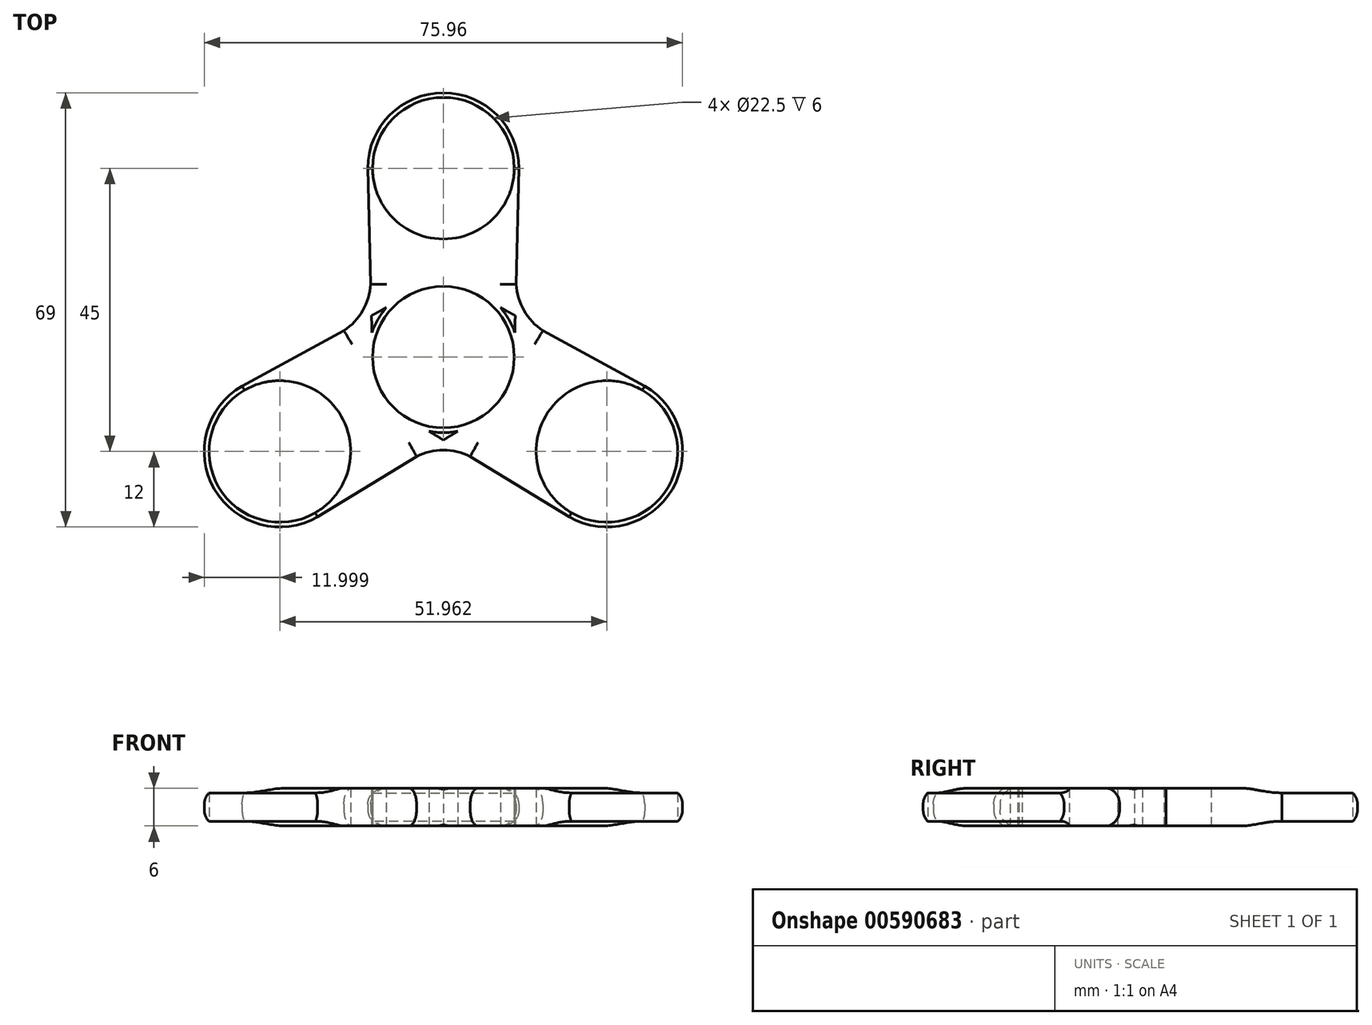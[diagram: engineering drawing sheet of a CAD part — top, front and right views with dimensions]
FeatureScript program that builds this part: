
annotation { "Feature Type Name" : "Feature", "Feature Type Description" : "" }
export const myFeature = defineFeature(function(context is Context, id is Id, definition is map)
    precondition{}
    {
        {
            var Q0;
            Q0=qCreatedBy(makeId("Top.planeOp"),FACE);
            var sketch = newSketch(context, id + "F0", { "sketchPlane" : qUnion([Q0])});
            skCircle(sketch, "E0", {"center": v(0, 0) * mm, "radius": 11.25 * mm});
            skCircle(sketch, "E1", {"center": v(0, 0) * mm, "radius": 12 * mm});
            skLineSegment(sketch, "E2", {"start": v(0, 0) * mm, "end": v(0, 12) * mm, "construction": true});
            skCircle(sketch, "E3", {"center": v(0, 30) * mm, "radius": 11.25 * mm});
            skArc(sketch, "E4", {"start": v(11.99, 29.4) * mm, "mid": v(0, 42) * mm, "end": v(-11.99, 29.4) * mm});
            skLineSegment(sketch, "E5", {"start": v(-11.25, 30) * mm, "end": v(-12, 30) * mm, "construction": true});
            skLineSegment(sketch, "E6", {"start": v(-12, 30) * mm, "end": v(-11.25, 30) * mm, "construction": true});
            skLineSegment(sketch, "E7", {"start": v(-11.25, 0) * mm, "end": v(-12, 30) * mm});
            skLineSegment(sketch, "E8", {"start": v(11.25, 0) * mm, "end": v(12, 30) * mm});
            skLineSegment(sketch, "E9.trimOffspring", {"start": v(11.25, 30) * mm, "end": v(12, 30) * mm, "construction": true});
            skLineSegment(sketch, "E10", {"start": v(0, 0) * mm, "end": v(9.74, -5.63) * mm, "construction": true});
            skLineSegment(sketch, "E11", {"start": v(0, 0) * mm, "end": v(-9.74, -5.62) * mm, "construction": true});
            skLineSegment(sketch, "E12", {"start": v(0, 0) * mm, "end": v(10.4, -6) * mm, "construction": true});
            skCircle(sketch, "E13", {"center": v(25.98, -15) * mm, "radius": 11.25 * mm});
            skArc(sketch, "E14", {"start": v(19.98, -25.4) * mm, "mid": v(36.52, -20.74) * mm, "end": v(31.45, -4.32) * mm});
            skLineSegment(sketch, "E15", {"start": v(31.6, -5.26) * mm, "end": v(31.98, -4.6) * mm, "construction": true});
            skLineSegment(sketch, "E16", {"start": v(31.98, -4.6) * mm, "end": v(31.6, -5.26) * mm, "construction": true});
            skLineSegment(sketch, "E17", {"start": v(0, 0) * mm, "end": v(11.25, 0) * mm, "construction": true});
            skLineSegment(sketch, "E18", {"start": v(0, 0) * mm, "end": v(-5.63, -9.74) * mm, "construction": true});
            skLineSegment(sketch, "E19", {"start": v(-5.63, -9.74) * mm, "end": v(5.63, 9.74) * mm, "construction": true});
            skLineSegment(sketch, "E20", {"start": v(5.62, 9.74) * mm, "end": v(31.98, -4.6) * mm});
            skLineSegment(sketch, "E21", {"start": v(-5.63, -9.74) * mm, "end": v(19.98, -25.4) * mm});
            skLineSegment(sketch, "E22.trimOffspring", {"start": v(20.36, -24.74) * mm, "end": v(19.98, -25.4) * mm, "construction": true});
            skLineSegment(sketch, "E23", {"start": v(0, 0) * mm, "end": v(-25.98, -15) * mm, "construction": true});
            skLineSegment(sketch, "E24", {"start": v(0, 0) * mm, "end": v(0, 30) * mm, "construction": true});
            skLineSegment(sketch, "E25", {"start": v(0, 0) * mm, "end": v(25.98, -15) * mm, "construction": true});
            skCircle(sketch, "E26", {"center": v(-25.98, -15) * mm, "radius": 11.25 * mm});
            skCircle(sketch, "E27", {"center": v(-25.98, -15) * mm, "radius": 12 * mm});
            skLineSegment(sketch, "E28", {"start": v(0, 0) * mm, "end": v(-5.62, 9.74) * mm, "construction": true});
            skLineSegment(sketch, "E29", {"start": v(-5.62, 9.74) * mm, "end": v(5.62, -9.74) * mm, "construction": true});
            skLineSegment(sketch, "E30", {"start": v(-25.98, -15) * mm, "end": v(-19.98, -25.4) * mm, "construction": true});
            skLineSegment(sketch, "E31", {"start": v(-25.98, -15) * mm, "end": v(-31.98, -4.6) * mm, "construction": true});
            skLineSegment(sketch, "E32", {"start": v(5.63, -9.74) * mm, "end": v(-19.98, -25.4) * mm});
            skLineSegment(sketch, "E33", {"start": v(-31.98, -4.6) * mm, "end": v(-5.63, 9.74) * mm});
            skLineSegment(sketch, "E34", {"start": v(-11.41, 6.6) * mm, "end": v(-11.54, 11.59) * mm, "construction": true});
            skLineSegment(sketch, "E35", {"start": v(-11.41, 6.6) * mm, "end": v(-15.8, 4.2) * mm, "construction": true});
            skLineSegment(sketch, "E36", {"start": v(11.41, 6.6) * mm, "end": v(11.54, 11.59) * mm, "construction": true});
            skLineSegment(sketch, "E37", {"start": v(11.41, 6.6) * mm, "end": v(15.8, 4.2) * mm, "construction": true});
            skLineSegment(sketch, "E38", {"start": v(0, -13.18) * mm, "end": v(-4.27, -15.79) * mm, "construction": true});
            skLineSegment(sketch, "E39", {"start": v(0, -13.18) * mm, "end": v(4.27, -15.79) * mm, "construction": true});
            skArc(sketch, "E40", {"start": v(-15.8, 4.2) * mm, "mid": v(-12.81, 7.4) * mm, "end": v(-11.54, 11.59) * mm});
            skPoint(sketch, "E41.end.orphan", {"position": v(-12.81, 7.4) * mm});
            skPoint(sketch, "E42.end.orphan", {"position": v(-13.67, 7.9) * mm});
            skArc(sketch, "E43", {"start": v(11.54, 11.59) * mm, "mid": v(12.81, 7.4) * mm, "end": v(15.8, 4.2) * mm});
            skPoint(sketch, "E44.end.orphan", {"position": v(12.81, 7.4) * mm});
            skPoint(sketch, "E45.start.orphan", {"position": v(13.67, 7.9) * mm});
            skArc(sketch, "E46", {"start": v(4.27, -15.79) * mm, "mid": v(0, -14.8) * mm, "end": v(-4.27, -15.79) * mm});
            skPoint(sketch, "E47.start.orphan", {"position": v(0, -15.79) * mm});
            skSolve(sketch);
        }
        {
            var Q0;
            Q0=makeQuery(id+"F0.imprint","IMPRINT",FACE,{"disambiguationData":[TD([[makeQuery(id+"F0.imprint","IMPRINT",EDGE,{"derivedFrom":sQuery(id+"F0.wireOp",EDGE,"E13")}),-1.0]])]});
            var Q1;
            {var subQ7=sQuery(id+"F0.wireOp",EDGE,"E1");var subQ9=sQuery(id+"F0.wireOp",EDGE,"E7");var subQ11=makeQuery(id+"F0.imprint","INTERSECT",VERTEX,{"derivedFrom":[subQ7,subQ9]});Q1=makeQuery(id+"F0.imprint","IMPRINT",FACE,{"disambiguationData":[TD([[makeQuery(id+"F0.imprint","IMPRINT",EDGE,{"disambiguationData":[TD([[subQ11,-1.0]])],"derivedFrom":subQ7}),-1.0]])]});}
            var Q2;
            Q2=makeQuery(id+"F0.imprint","IMPRINT",FACE,{"disambiguationData":[TD([[makeQuery(id+"F0.imprint","IMPRINT",EDGE,{"derivedFrom":sQuery(id+"F0.wireOp",EDGE,"E3")}),-1.0]])]});
            var Q3;
            Q3=makeQuery(id+"F0.imprint","IMPRINT",FACE,{"disambiguationData":[TD([[makeQuery(id+"F0.imprint","IMPRINT",EDGE,{"derivedFrom":sQuery(id+"F0.wireOp",EDGE,"E26")}),-1.0]])]});
            var Q4;
            {var subQ0=sQuery(id+"F0.wireOp",EDGE,"LzCppDYF-5cjn-ystm-teWX-WIOvTmqxfPc8");Q4=makeQuery(id+"F0.imprint","IMPRINT",FACE,{"disambiguationData":[TD([[makeQuery(id+"F0.imprint","IMPRINT",EDGE,{"derivedFrom":subQ0}),-1.0]])]});}
            var Q5;
            {var subQ0=sQuery(id+"F0.wireOp",EDGE,"E45");Q5=makeQuery(id+"F0.imprint","IMPRINT",FACE,{"disambiguationData":[TD([[makeQuery(id+"F0.imprint","IMPRINT",EDGE,{"derivedFrom":subQ0}),-1.0]])]});}
            var Q6;
            {var subQ0=sQuery(id+"F0.wireOp",EDGE,"dLhTZdyE-zlHB-rUEX-3xYo-1x3OKXFwP9mY");Q6=makeQuery(id+"F0.imprint","IMPRINT",FACE,{"disambiguationData":[TD([[makeQuery(id+"F0.imprint","IMPRINT",EDGE,{"derivedFrom":subQ0}),1.0]])]});}
            var Q7;
            {var subQ0=sQuery(id+"F0.wireOp",EDGE,"E46");Q7=makeQuery(id+"F0.imprint","IMPRINT",FACE,{"disambiguationData":[TD([[makeQuery(id+"F0.imprint","IMPRINT",EDGE,{"derivedFrom":subQ0}),-1.0]])]});}
            var Q8;
            {var subQ0=sQuery(id+"F0.wireOp",EDGE,"E40");Q8=makeQuery(id+"F0.imprint","IMPRINT",FACE,{"disambiguationData":[TD([[makeQuery(id+"F0.imprint","IMPRINT",EDGE,{"derivedFrom":subQ0}),-1.0]])]});}
            var Q9;
            {var subQ0=sQuery(id+"F0.wireOp",EDGE,"E43");Q9=makeQuery(id+"F0.imprint","IMPRINT",FACE,{"disambiguationData":[TD([[makeQuery(id+"F0.imprint","IMPRINT",EDGE,{"derivedFrom":subQ0}),-1.0]])]});}
            var Q10;
            {var subQ0=sQuery(id+"F0.wireOp",EDGE,"E7");var subQ1=sQuery(id+"F0.wireOp",EDGE,"E0");var subQ2=makeQuery(id+"F0.imprint","INTERSECT",VERTEX,{"derivedFrom":[subQ1,subQ0]});Q10=makeQuery(id+"F0.imprint","IMPRINT",FACE,{"disambiguationData":[TD([[makeQuery(id+"F0.imprint","IMPRINT",EDGE,{"disambiguationData":[TD([[subQ2,-1.0]])],"derivedFrom":subQ1}),-1.0]])]});}
            var Q11;
            {var subQ0=sQuery(id+"F0.wireOp",EDGE,"E7");var subQ1=sQuery(id+"F0.wireOp",EDGE,"E0");var subQ2=makeQuery(id+"F0.imprint","INTERSECT",VERTEX,{"derivedFrom":[subQ1,subQ0]});Q11=makeQuery(id+"F0.imprint","IMPRINT",FACE,{"disambiguationData":[TD([[makeQuery(id+"F0.imprint","IMPRINT",EDGE,{"disambiguationData":[TD([[subQ2,1.0]])],"derivedFrom":subQ1}),-1.0]])]});}
            var Q12;
            {var subQ0=sQuery(id+"F0.wireOp",EDGE,"E20");var subQ1=sQuery(id+"F0.wireOp",EDGE,"E0");var subQ2=makeQuery(id+"F0.imprint","INTERSECT",VERTEX,{"derivedFrom":[subQ1,subQ0]});Q12=makeQuery(id+"F0.imprint","IMPRINT",FACE,{"disambiguationData":[TD([[makeQuery(id+"F0.imprint","IMPRINT",EDGE,{"disambiguationData":[TD([[subQ2,-1.0]])],"derivedFrom":subQ1}),-1.0]])]});}
            var Q13;
            {var subQ0=sQuery(id+"F0.wireOp",EDGE,"E8");var subQ1=sQuery(id+"F0.wireOp",EDGE,"E0");var subQ2=makeQuery(id+"F0.imprint","INTERSECT",VERTEX,{"derivedFrom":[subQ1,subQ0]});Q13=makeQuery(id+"F0.imprint","IMPRINT",FACE,{"disambiguationData":[TD([[makeQuery(id+"F0.imprint","IMPRINT",EDGE,{"disambiguationData":[TD([[subQ2,-1.0]])],"derivedFrom":subQ1}),-1.0]])]});}
            var Q14;
            {var subQ0=sQuery(id+"F0.wireOp",EDGE,"E8");var subQ1=sQuery(id+"F0.wireOp",EDGE,"E0");var subQ2=makeQuery(id+"F0.imprint","INTERSECT",VERTEX,{"derivedFrom":[subQ1,subQ0]});Q14=makeQuery(id+"F0.imprint","IMPRINT",FACE,{"disambiguationData":[TD([[makeQuery(id+"F0.imprint","IMPRINT",EDGE,{"disambiguationData":[TD([[subQ2,1.0]])],"derivedFrom":subQ1}),-1.0]])]});}
            var Q15;
            {var subQ0=sQuery(id+"F0.wireOp",EDGE,"E21");var subQ1=sQuery(id+"F0.wireOp",EDGE,"E0");var subQ2=makeQuery(id+"F0.imprint","INTERSECT",VERTEX,{"derivedFrom":[subQ1,subQ0]});Q15=makeQuery(id+"F0.imprint","IMPRINT",FACE,{"disambiguationData":[TD([[makeQuery(id+"F0.imprint","IMPRINT",EDGE,{"disambiguationData":[TD([[subQ2,-1.0]])],"derivedFrom":subQ1}),-1.0]])]});}
            extrude(context, id + "F1", {"entities" : qUnion([Q0, Q1, Q2, Q3, Q4, Q5, Q6, Q7, Q8, Q9, Q10, Q11, Q12, Q13, Q14, Q15]), "depth" : 6 * mm, "offsetDistance" : 25.4 * mm});
        }
        {
            var Q0;
            {var subQ0=sQuery(id+"F0.wireOp",EDGE,"E33");var subQ1=sQuery(id+"F0.wireOp",EDGE,"E27");Q0=makeQuery(id+"F1.opExtrude","CAP_EDGE",EDGE,{"disambiguationData":[OSD([subQ0]),TDD([makeQuery(id+"F0.imprint","IMPRINT",EDGE,{"disambiguationData":[TD([[makeQuery(id+"F0.imprint","INTERSECT",VERTEX,{"disambiguationData":[OD(0.0)],"derivedFrom":[subQ1,subQ0]}),-1.0]])],"derivedFrom":subQ0}),makeQuery(id+"F0.imprint","IMPRINT",EDGE,{"disambiguationData":[TD([[makeQuery(id+"F0.imprint","INTERSECT",VERTEX,{"derivedFrom":[subQ0,sQuery(id+"F0.wireOp",EDGE,"E40")]}),1.0]])],"derivedFrom":subQ0})])],"isStart":false});}
            var Q1;
            Q1=makeQuery(id+"F1.opExtrude","CAP_EDGE",EDGE,{"disambiguationData":[OSD([sQuery(id+"F0.wireOp",EDGE,"E40")])],"isStart":false});
            var Q2;
            {var subQ0=sQuery(id+"F0.wireOp",EDGE,"E7");var subQ1=sQuery(id+"F0.wireOp",EDGE,"E4");var subQ2=makeQuery(id+"F0.imprint","INTERSECT",VERTEX,{"disambiguationData":[OD(0.0)],"derivedFrom":[subQ1,subQ0]});Q2=makeQuery(id+"F1.opExtrude","CAP_EDGE",EDGE,{"disambiguationData":[OSD([subQ0]),TDD([makeQuery(id+"F0.imprint","IMPRINT",EDGE,{"disambiguationData":[TD([[subQ2,1.0]])],"derivedFrom":subQ0}),makeQuery(id+"F0.imprint","IMPRINT",EDGE,{"disambiguationData":[TD([[subQ2,-1.0]])],"derivedFrom":subQ0})])],"isStart":false});}
            var Q3;
            Q3=makeQuery(id+"F1.opExtrude","CAP_EDGE",EDGE,{"disambiguationData":[OSD([sQuery(id+"F0.wireOp",EDGE,"E4")])],"isStart":false});
            var Q4;
            {var subQ0=sQuery(id+"F0.wireOp",EDGE,"E8");var subQ1=sQuery(id+"F0.wireOp",EDGE,"E4");var subQ2=makeQuery(id+"F0.imprint","INTERSECT",VERTEX,{"disambiguationData":[OD(0.0)],"derivedFrom":[subQ1,subQ0]});Q4=makeQuery(id+"F1.opExtrude","CAP_EDGE",EDGE,{"disambiguationData":[OSD([subQ0]),TDD([makeQuery(id+"F0.imprint","IMPRINT",EDGE,{"disambiguationData":[TD([[subQ2,1.0]])],"derivedFrom":subQ0}),makeQuery(id+"F0.imprint","IMPRINT",EDGE,{"disambiguationData":[TD([[subQ2,-1.0]])],"derivedFrom":subQ0})])],"isStart":false});}
            var Q5;
            Q5=makeQuery(id+"F1.opExtrude","CAP_EDGE",EDGE,{"disambiguationData":[OSD([sQuery(id+"F0.wireOp",EDGE,"E43")])],"isStart":false});
            var Q6;
            {var subQ0=sQuery(id+"F0.wireOp",EDGE,"E20");var subQ1=sQuery(id+"F0.wireOp",EDGE,"E14");var subQ2=makeQuery(id+"F0.imprint","INTERSECT",VERTEX,{"disambiguationData":[OD(0.0)],"derivedFrom":[subQ1,subQ0]});Q6=makeQuery(id+"F1.opExtrude","CAP_EDGE",EDGE,{"disambiguationData":[OSD([subQ0]),TDD([makeQuery(id+"F0.imprint","IMPRINT",EDGE,{"disambiguationData":[TD([[subQ2,1.0]])],"derivedFrom":subQ0}),makeQuery(id+"F0.imprint","IMPRINT",EDGE,{"disambiguationData":[TD([[subQ2,-1.0]])],"derivedFrom":subQ0})])],"isStart":false});}
            var Q7;
            Q7=makeQuery(id+"F1.opExtrude","CAP_EDGE",EDGE,{"disambiguationData":[OSD([sQuery(id+"F0.wireOp",EDGE,"E14")])],"isStart":false});
            var Q8;
            {var subQ0=sQuery(id+"F0.wireOp",EDGE,"E21");Q8=makeQuery(id+"F1.opExtrude","CAP_EDGE",EDGE,{"disambiguationData":[OSD([subQ0]),TDD([makeQuery(id+"F0.imprint","IMPRINT",EDGE,{"disambiguationData":[TD([[makeQuery(id+"F0.imprint","INTERSECT",VERTEX,{"derivedFrom":[sQuery(id+"F0.wireOp",EDGE,"E14"),subQ0]}),1.0]])],"derivedFrom":subQ0})])],"isStart":false});}
            var Q9;
            Q9=makeQuery(id+"F1.opExtrude","CAP_EDGE",EDGE,{"disambiguationData":[OSD([sQuery(id+"F0.wireOp",EDGE,"E46")])],"isStart":false});
            var Q10;
            {var subQ0=sQuery(id+"F0.wireOp",EDGE,"E32");var subQ1=sQuery(id+"F0.wireOp",EDGE,"E27");Q10=makeQuery(id+"F1.opExtrude","CAP_EDGE",EDGE,{"disambiguationData":[OSD([subQ0]),TDD([makeQuery(id+"F0.imprint","IMPRINT",EDGE,{"disambiguationData":[TD([[makeQuery(id+"F0.imprint","INTERSECT",VERTEX,{"derivedFrom":[subQ0,sQuery(id+"F0.wireOp",EDGE,"E46")]}),-1.0]])],"derivedFrom":subQ0}),makeQuery(id+"F0.imprint","IMPRINT",EDGE,{"disambiguationData":[TD([[makeQuery(id+"F0.imprint","INTERSECT",VERTEX,{"disambiguationData":[OD(0.0)],"derivedFrom":[subQ1,subQ0]}),1.0]])],"derivedFrom":subQ0})])],"isStart":false});}
            var Q11;
            Q11=makeQuery(id+"F1.opExtrude","CAP_EDGE",EDGE,{"disambiguationData":[OSD([sQuery(id+"F0.wireOp",EDGE,"E27")])],"isStart":false});
            var Q12;
            Q12=makeQuery(id+"F1.opExtrude","CAP_EDGE",EDGE,{"disambiguationData":[OSD([sQuery(id+"F0.wireOp",EDGE,"E4")])],"isStart":true});
            var Q13;
            {var subQ0=sQuery(id+"F0.wireOp",EDGE,"E7");var subQ1=sQuery(id+"F0.wireOp",EDGE,"E4");var subQ2=makeQuery(id+"F0.imprint","INTERSECT",VERTEX,{"disambiguationData":[OD(0.0)],"derivedFrom":[subQ1,subQ0]});Q13=makeQuery(id+"F1.opExtrude","CAP_EDGE",EDGE,{"disambiguationData":[OSD([subQ0]),TDD([makeQuery(id+"F0.imprint","IMPRINT",EDGE,{"disambiguationData":[TD([[subQ2,1.0]])],"derivedFrom":subQ0}),makeQuery(id+"F0.imprint","IMPRINT",EDGE,{"disambiguationData":[TD([[subQ2,-1.0]])],"derivedFrom":subQ0})])],"isStart":true});}
            var Q14;
            Q14=makeQuery(id+"F1.opExtrude","CAP_EDGE",EDGE,{"disambiguationData":[OSD([sQuery(id+"F0.wireOp",EDGE,"E40")])],"isStart":true});
            var Q15;
            {var subQ0=sQuery(id+"F0.wireOp",EDGE,"E33");var subQ1=sQuery(id+"F0.wireOp",EDGE,"E27");Q15=makeQuery(id+"F1.opExtrude","CAP_EDGE",EDGE,{"disambiguationData":[OSD([subQ0]),TDD([makeQuery(id+"F0.imprint","IMPRINT",EDGE,{"disambiguationData":[TD([[makeQuery(id+"F0.imprint","INTERSECT",VERTEX,{"disambiguationData":[OD(0.0)],"derivedFrom":[subQ1,subQ0]}),-1.0]])],"derivedFrom":subQ0}),makeQuery(id+"F0.imprint","IMPRINT",EDGE,{"disambiguationData":[TD([[makeQuery(id+"F0.imprint","INTERSECT",VERTEX,{"derivedFrom":[subQ0,sQuery(id+"F0.wireOp",EDGE,"E40")]}),1.0]])],"derivedFrom":subQ0})])],"isStart":true});}
            var Q16;
            Q16=makeQuery(id+"F1.opExtrude","CAP_EDGE",EDGE,{"disambiguationData":[OSD([sQuery(id+"F0.wireOp",EDGE,"E27")])],"isStart":true});
            var Q17;
            {var subQ0=sQuery(id+"F0.wireOp",EDGE,"E32");var subQ1=sQuery(id+"F0.wireOp",EDGE,"E27");Q17=makeQuery(id+"F1.opExtrude","CAP_EDGE",EDGE,{"disambiguationData":[OSD([subQ0]),TDD([makeQuery(id+"F0.imprint","IMPRINT",EDGE,{"disambiguationData":[TD([[makeQuery(id+"F0.imprint","INTERSECT",VERTEX,{"derivedFrom":[subQ0,sQuery(id+"F0.wireOp",EDGE,"E46")]}),-1.0]])],"derivedFrom":subQ0}),makeQuery(id+"F0.imprint","IMPRINT",EDGE,{"disambiguationData":[TD([[makeQuery(id+"F0.imprint","INTERSECT",VERTEX,{"disambiguationData":[OD(0.0)],"derivedFrom":[subQ1,subQ0]}),1.0]])],"derivedFrom":subQ0})])],"isStart":true});}
            var Q18;
            Q18=makeQuery(id+"F1.opExtrude","CAP_EDGE",EDGE,{"disambiguationData":[OSD([sQuery(id+"F0.wireOp",EDGE,"E46")])],"isStart":true});
            var Q19;
            {var subQ0=sQuery(id+"F0.wireOp",EDGE,"E21");Q19=makeQuery(id+"F1.opExtrude","CAP_EDGE",EDGE,{"disambiguationData":[OSD([subQ0]),TDD([makeQuery(id+"F0.imprint","IMPRINT",EDGE,{"disambiguationData":[TD([[makeQuery(id+"F0.imprint","INTERSECT",VERTEX,{"derivedFrom":[sQuery(id+"F0.wireOp",EDGE,"E14"),subQ0]}),1.0]])],"derivedFrom":subQ0})])],"isStart":true});}
            var Q20;
            Q20=makeQuery(id+"F1.opExtrude","CAP_EDGE",EDGE,{"disambiguationData":[OSD([sQuery(id+"F0.wireOp",EDGE,"E14")])],"isStart":true});
            var Q21;
            {var subQ0=sQuery(id+"F0.wireOp",EDGE,"E20");var subQ1=sQuery(id+"F0.wireOp",EDGE,"E14");var subQ2=makeQuery(id+"F0.imprint","INTERSECT",VERTEX,{"disambiguationData":[OD(0.0)],"derivedFrom":[subQ1,subQ0]});Q21=makeQuery(id+"F1.opExtrude","CAP_EDGE",EDGE,{"disambiguationData":[OSD([subQ0]),TDD([makeQuery(id+"F0.imprint","IMPRINT",EDGE,{"disambiguationData":[TD([[subQ2,1.0]])],"derivedFrom":subQ0}),makeQuery(id+"F0.imprint","IMPRINT",EDGE,{"disambiguationData":[TD([[subQ2,-1.0]])],"derivedFrom":subQ0})])],"isStart":true});}
            var Q22;
            Q22=makeQuery(id+"F1.opExtrude","CAP_EDGE",EDGE,{"disambiguationData":[OSD([sQuery(id+"F0.wireOp",EDGE,"E43")])],"isStart":true});
            var Q23;
            {var subQ0=sQuery(id+"F0.wireOp",EDGE,"E8");var subQ1=sQuery(id+"F0.wireOp",EDGE,"E4");var subQ2=makeQuery(id+"F0.imprint","INTERSECT",VERTEX,{"disambiguationData":[OD(0.0)],"derivedFrom":[subQ1,subQ0]});Q23=makeQuery(id+"F1.opExtrude","CAP_EDGE",EDGE,{"disambiguationData":[OSD([subQ0]),TDD([makeQuery(id+"F0.imprint","IMPRINT",EDGE,{"disambiguationData":[TD([[subQ2,1.0]])],"derivedFrom":subQ0}),makeQuery(id+"F0.imprint","IMPRINT",EDGE,{"disambiguationData":[TD([[subQ2,-1.0]])],"derivedFrom":subQ0})])],"isStart":true});}
            fillet(context, id + "F2", {"entities" : qUnion([Q0, Q1, Q2, Q3, Q4, Q5, Q6, Q7, Q8, Q9, Q10, Q11, Q12, Q13, Q14, Q15, Q16, Q17, Q18, Q19, Q20, Q21, Q22, Q23]), "radius" : 2.54 * mm, "tangentPropagation" : true, "allowEdgeOverflow" : false});
        }
    });
